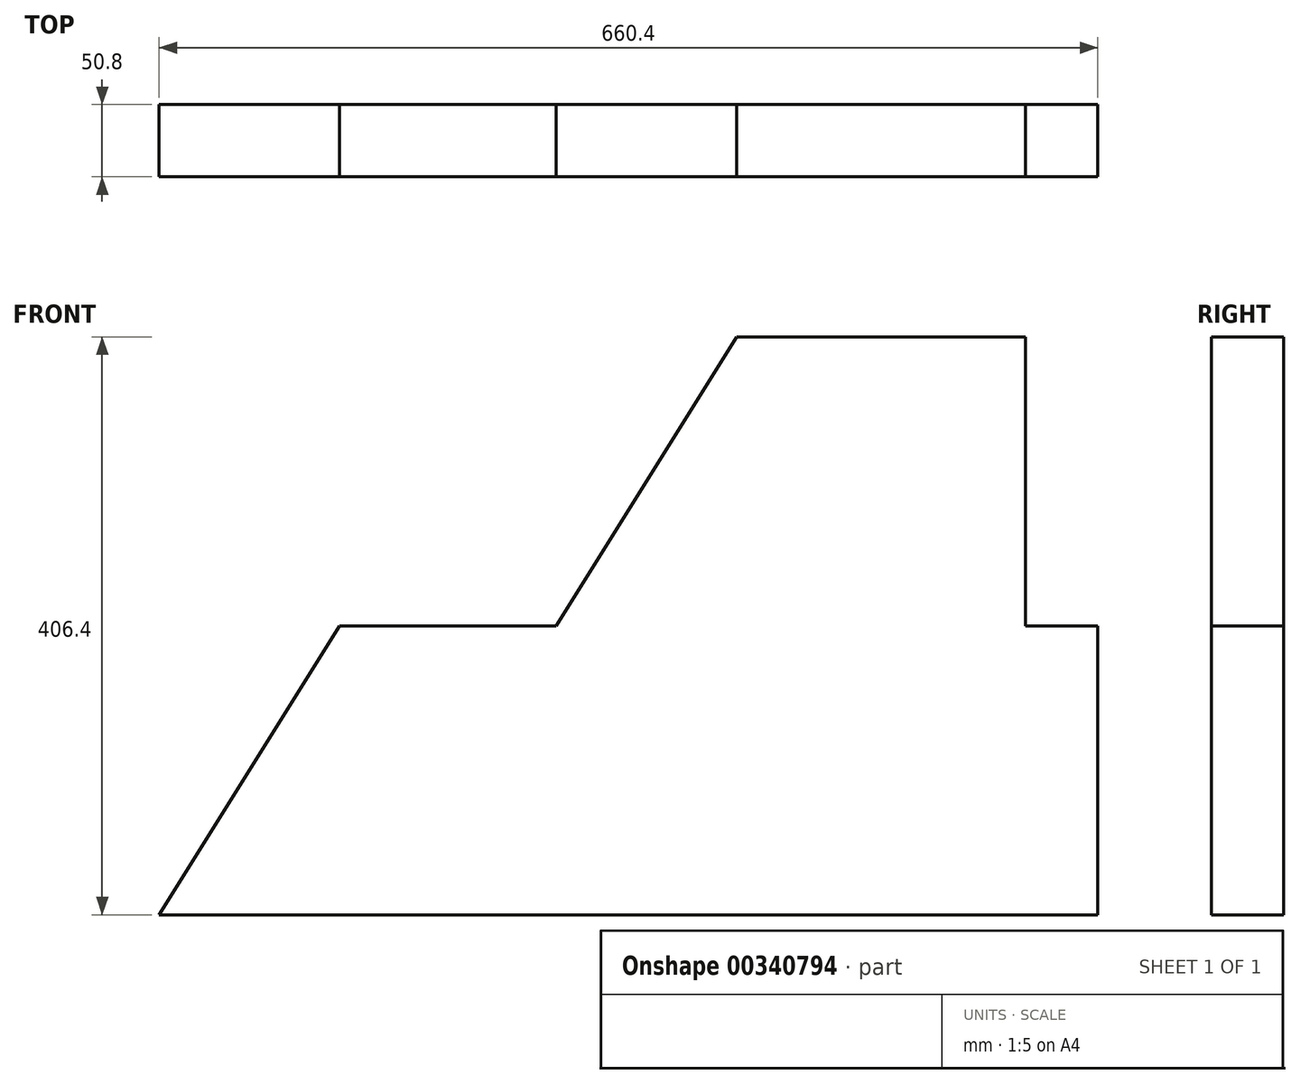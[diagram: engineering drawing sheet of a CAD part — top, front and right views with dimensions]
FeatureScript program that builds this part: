
annotation { "Feature Type Name" : "Feature", "Feature Type Description" : "" }
export const myFeature = defineFeature(function(context is Context, id is Id, definition is map)
    precondition{}
    {
        {
            var Q0;
            Q0=qCreatedBy(makeId("Front.planeOp"),FACE);
            var sketch = newSketch(context, id + "F0", { "sketchPlane" : qUnion([Q0])});
            skLineSegment(sketch, "E0", {"start": v(0, 0) * mm, "end": v(660.4, 0) * mm});
            skLineSegment(sketch, "E1", {"start": v(660.4, 0) * mm, "end": v(660.4, 203.2) * mm});
            skLineSegment(sketch, "E2", {"start": v(660.4, 203.2) * mm, "end": v(609.6, 203.2) * mm});
            skLineSegment(sketch, "E3", {"start": v(609.6, 203.2) * mm, "end": v(609.6, 406.4) * mm});
            skLineSegment(sketch, "E4", {"start": v(609.6, 406.4) * mm, "end": v(406.4, 406.4) * mm});
            skLineSegment(sketch, "E5", {"start": v(406.4, 406.4) * mm, "end": v(279.4, 203.2) * mm});
            skLineSegment(sketch, "E6", {"start": v(279.4, 203.2) * mm, "end": v(127, 203.2) * mm});
            skLineSegment(sketch, "E7", {"start": v(127, 203.2) * mm, "end": v(0, 0) * mm});
            skSolve(sketch);
        }
        {
            var Q0;
            Q0=makeQuery(id+"F0.imprint","IMPRINT",FACE,{"disambiguationData":[TD([[makeQuery(id+"F0.imprint","IMPRINT",EDGE,{"derivedFrom":sQuery(id+"F0.wireOp",EDGE,"E0")}),1.0]])]});
            extrude(context, id + "F1", {"entities" : qUnion([Q0]), "depth" : 50.8 * mm});
        }
    });
